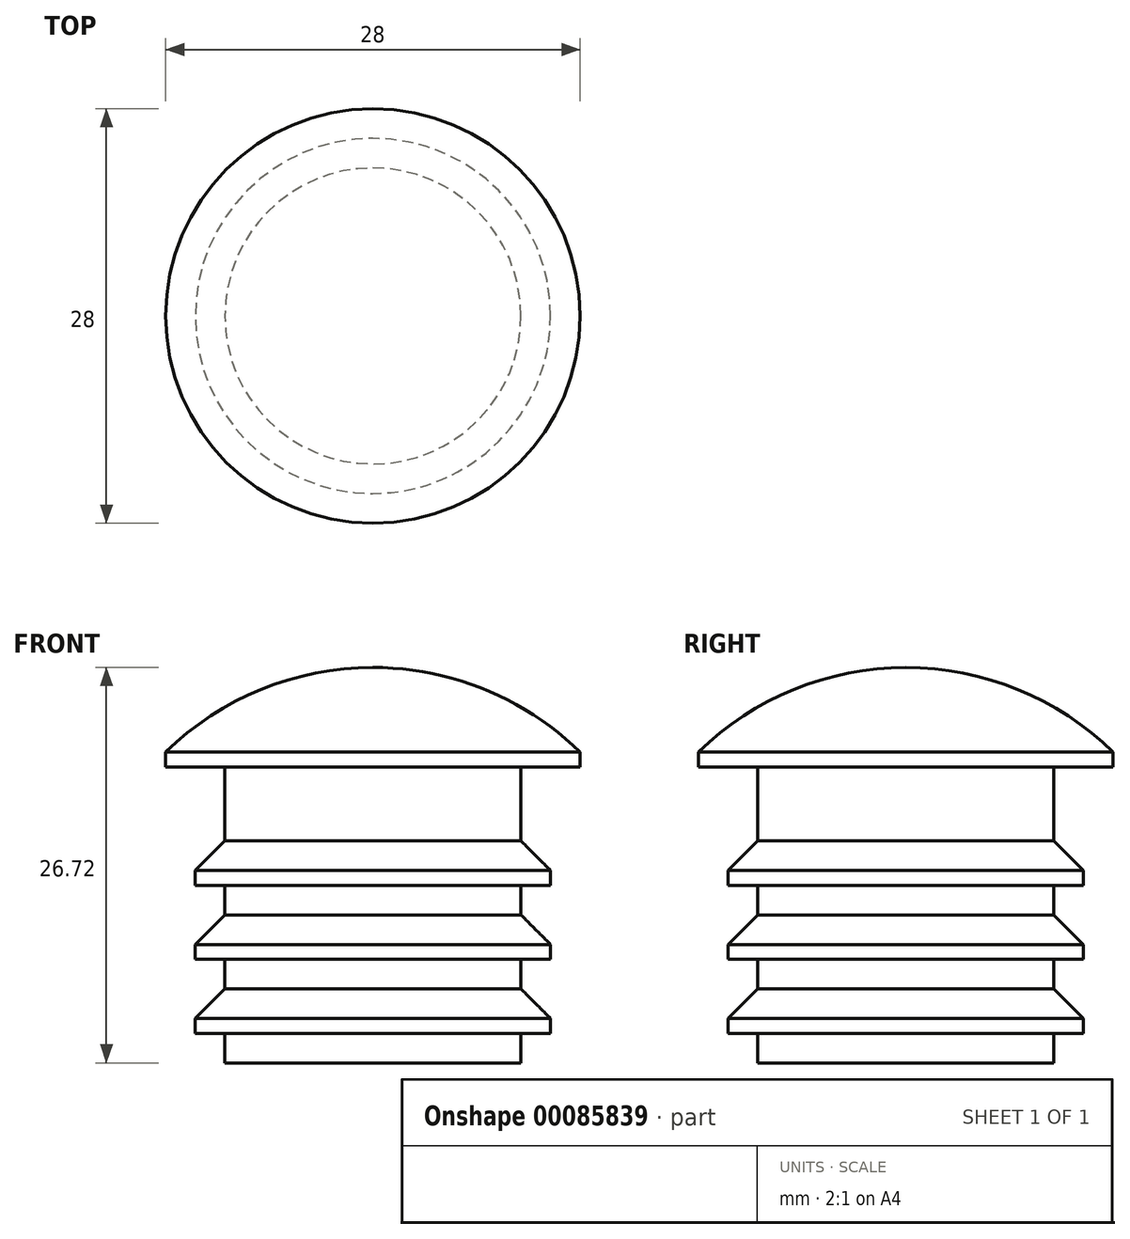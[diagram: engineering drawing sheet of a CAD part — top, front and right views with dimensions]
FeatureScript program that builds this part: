
annotation { "Feature Type Name" : "Feature", "Feature Type Description" : "" }
export const myFeature = defineFeature(function(context is Context, id is Id, definition is map)
    precondition{}
    {
        {
            var Q0;
            Q0=qCreatedBy(makeId("Front.planeOp"),FACE);
            var sketch = newSketch(context, id + "F0", { "sketchPlane" : qUnion([Q0])});
            skLineSegment(sketch, "E0", {"start": v(10, 11) * mm, "end": v(10, -9) * mm, "construction": true});
            skLineSegment(sketch, "E1", {"start": v(10, -9) * mm, "end": v(0, -9) * mm});
            skLineSegment(sketch, "E2", {"start": v(10, 11) * mm, "end": v(14, 11) * mm});
            skLineSegment(sketch, "E3", {"start": v(14, 11) * mm, "end": v(14, 12) * mm});
            skArc(sketch, "E4", {"start": v(14, 12) * mm, "mid": v(7.56, 16.23) * mm, "end": v(0, 17.72) * mm});
            skLineSegment(sketch, "E5", {"start": v(10, 6) * mm, "end": v(12, 4) * mm});
            skLineSegment(sketch, "E6", {"start": v(12, 4) * mm, "end": v(12, 3) * mm});
            skLineSegment(sketch, "E7", {"start": v(12, 3) * mm, "end": v(10, 3) * mm});
            skLineSegment(sketch, "E8.0.1.0", {"start": v(10, 1) * mm, "end": v(12, -1) * mm});
            skLineSegment(sketch, "E8.0.1.1", {"start": v(12, -1) * mm, "end": v(12, -2) * mm});
            skLineSegment(sketch, "E8.0.1.2", {"start": v(12, -2) * mm, "end": v(10, -2) * mm});
            skLineSegment(sketch, "E8.0.2.0", {"start": v(10, -4) * mm, "end": v(12, -6) * mm});
            skLineSegment(sketch, "E8.0.2.1", {"start": v(12, -6) * mm, "end": v(12, -7) * mm});
            skLineSegment(sketch, "E8.0.2.2", {"start": v(12, -7) * mm, "end": v(10, -7) * mm});
            skLineSegment(sketch, "E8.direction2", {"start": v(12, 4) * mm, "end": v(12, -1) * mm, "construction": true});
            skLineSegment(sketch, "E9", {"start": v(10, 6) * mm, "end": v(10, 11) * mm});
            skLineSegment(sketch, "E10", {"start": v(10, 3) * mm, "end": v(10, 1) * mm});
            skLineSegment(sketch, "E11", {"start": v(10, -2) * mm, "end": v(10, -4) * mm});
            skLineSegment(sketch, "E12", {"start": v(10, -7) * mm, "end": v(10, -9) * mm});
            skLineSegment(sketch, "E13", {"start": v(0, 17.72) * mm, "end": v(0, -9) * mm});
            skSolve(sketch);
        }
        {
            var Q0;
            Q0=makeQuery(id+"F0.imprint","IMPRINT",FACE,{"disambiguationData":[TD([[makeQuery(id+"F0.imprint","IMPRINT",EDGE,{"derivedFrom":sQuery(id+"F0.wireOp",EDGE,"E1")}),-1.0]])]});
            var Q1;
            Q1=sQuery(id+"F0.wireOp",EDGE,"E13");
            revolve(context, id + "F1", {"entities" : qUnion([Q0]), "axis" : qUnion([Q1]), "revolveType" : RevolveType.FULL});
        }
    });
